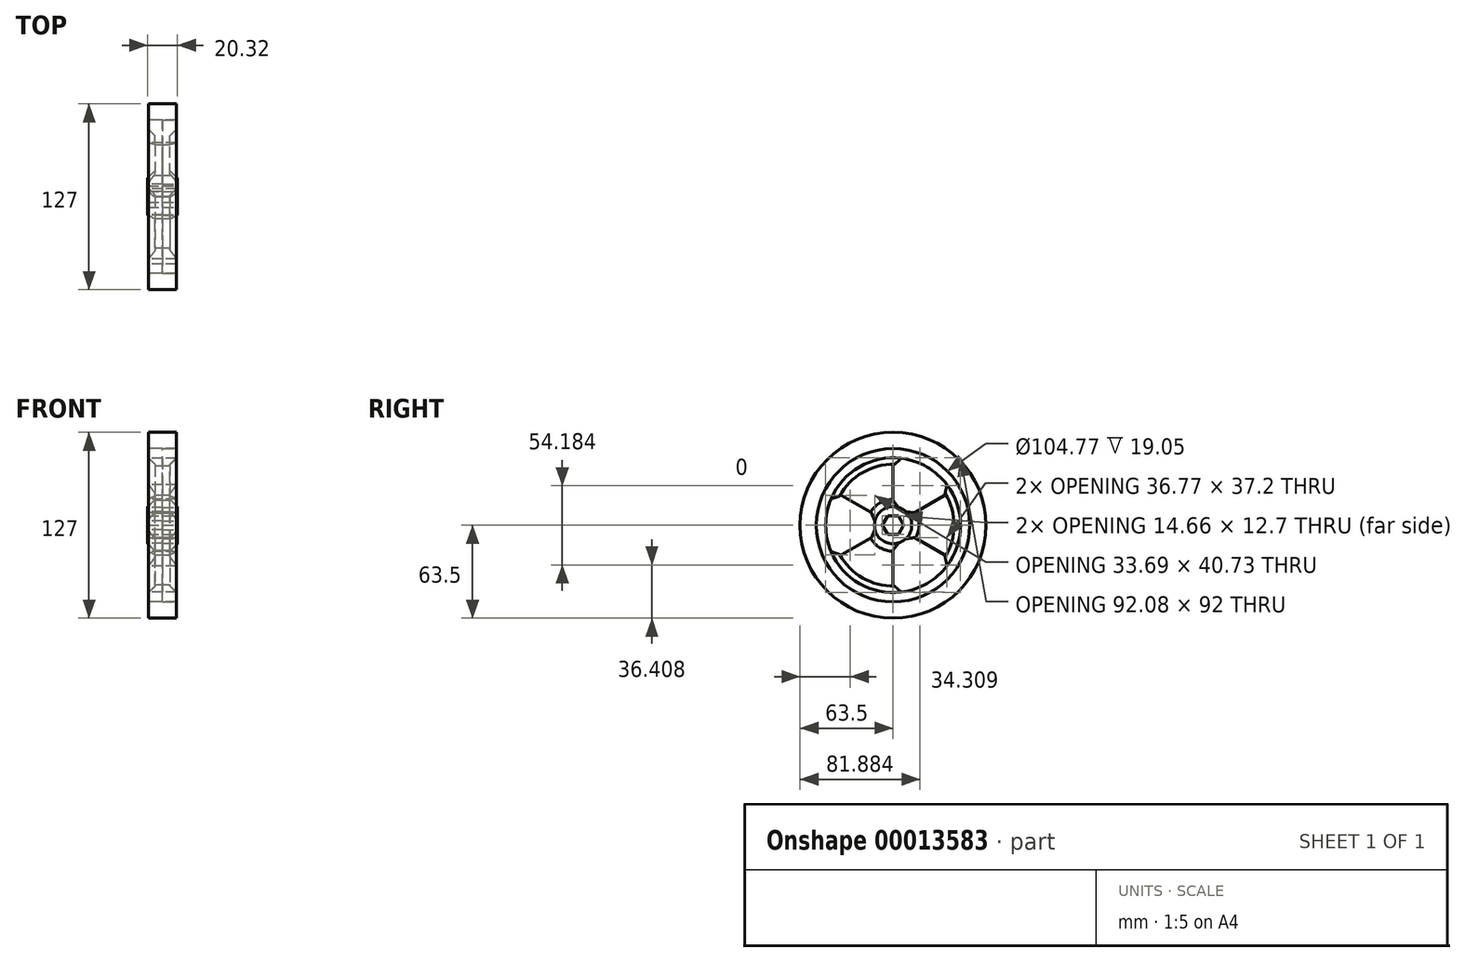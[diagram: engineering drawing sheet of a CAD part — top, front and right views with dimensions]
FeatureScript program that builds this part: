
annotation { "Feature Type Name" : "Feature", "Feature Type Description" : "" }
export const myFeature = defineFeature(function(context is Context, id is Id, definition is map)
    precondition{}
    {
        {
            var Q0;
            Q0=qCreatedBy(makeId("Front.planeOp"),FACE);
            var sketch = newSketch(context, id + "F0", { "sketchPlane" : qUnion([Q0])});
            skLineSegment(sketch, "E0", {"start": v(0, 0) * mm, "end": v(0, 52.39) * mm});
            skLineSegment(sketch, "E1", {"start": v(0, 52.39) * mm, "end": v(9.53, 52.39) * mm});
            skLineSegment(sketch, "E2", {"start": v(9.53, 52.39) * mm, "end": v(9.53, 46.04) * mm});
            skLineSegment(sketch, "E3", {"start": v(5.08, 41.6) * mm, "end": v(5.08, 12.7) * mm});
            skLineSegment(sketch, "E4", {"start": v(5.08, 12.7) * mm, "end": v(10.16, 12.7) * mm});
            skLineSegment(sketch, "E5", {"start": v(10.16, 12.7) * mm, "end": v(10.16, 0) * mm});
            skLineSegment(sketch, "E6", {"start": v(10.16, 0) * mm, "end": v(0, 0) * mm});
            skLineSegment(sketch, "E7", {"start": v(0, 0) * mm, "end": v(0, -52.39) * mm, "construction": true});
            skLineSegment(sketch, "E8", {"start": v(0, -52.39) * mm, "end": v(10.16, -52.39) * mm, "construction": true});
            skLineSegment(sketch, "E9", {"start": v(10.16, -52.39) * mm, "end": v(10.16, 0) * mm, "construction": true});
            skLineSegment(sketch, "E10", {"start": v(5.08, 41.6) * mm, "end": v(9.53, 46.04) * mm});
            skSolve(sketch);
        }
        {
            var Q0;
            Q0=makeQuery(id+"F0.imprint","IMPRINT",FACE,{"disambiguationData":[TD([[makeQuery(id+"F0.imprint","IMPRINT",EDGE,{"derivedFrom":sQuery(id+"F0.wireOp",EDGE,"E0")}),-1.0]])]});
            var Q1;
            Q1=sQuery(id+"F0.wireOp",EDGE,"E6");
            revolve(context, id + "F1", {"entities" : qUnion([Q0]), "axis" : qUnion([Q1]), "revolveType" : RevolveType.FULL});
        }
        {
            var Q0;
            Q0=makeQuery(id+"F1.opRevolve","SWEPT_BODY",BODY,{"disambiguationData":[OSD([sQuery(id+"F0.wireOp",EDGE,"E0"),sQuery(id+"F0.wireOp",EDGE,"E1"),sQuery(id+"F0.wireOp",EDGE,"E2"),sQuery(id+"F0.wireOp",EDGE,"E3"),sQuery(id+"F0.wireOp",EDGE,"E4"),sQuery(id+"F0.wireOp",EDGE,"E5"),sQuery(id+"F0.wireOp",EDGE,"E6"),sQuery(id+"F0.wireOp",EDGE,"E10")])]});
            var Q1;
            Q1=qCreatedBy(makeId("Right.planeOp"),FACE);
            mirror(context, id + "F2", {"entities" : qUnion([Q0]), "mirrorPlane" : qUnion([Q1])});
        }
        {
            var Q0;
            Q0=makeQuery(id+"F1.opRevolve","SWEPT_FACE",FACE,{"disambiguationData":[OSD([sQuery(id+"F0.wireOp",EDGE,"E5")])]});
            var sketch = newSketch(context, id + "F3", { "sketchPlane" : qUnion([Q0])});
            skCircle(sketch, "E11.cCircle", {"center": v(0, 0) * mm, "radius": 6.35 * mm, "construction": true});
            skLineSegment(sketch, "E11.0", {"start": v(3.67, -6.35) * mm, "end": v(-3.67, -6.35) * mm});
            skLineSegment(sketch, "E11.1", {"start": v(-3.67, -6.35) * mm, "end": v(-7.33, 0) * mm});
            skLineSegment(sketch, "E11.2", {"start": v(-7.33, 0) * mm, "end": v(-3.67, 6.35) * mm});
            skLineSegment(sketch, "E11.3", {"start": v(-3.67, 6.35) * mm, "end": v(3.67, 6.35) * mm});
            skLineSegment(sketch, "E11.4", {"start": v(3.67, 6.35) * mm, "end": v(7.33, 0) * mm});
            skLineSegment(sketch, "E11.5", {"start": v(7.33, 0) * mm, "end": v(3.67, -6.35) * mm});
            skPoint(sketch, "E11.0.midPoint", {"position": v(0, -6.35) * mm});
            skSolve(sketch);
        }
        {
            var Q0;
            Q0 = qSketchRegion(id + "F3", true);
            extrude(context, id + "F4", {"entities" : qUnion([Q0]), "operationType" : NewBodyOperationType.REMOVE, "endBound" : BoundingType.THROUGH_ALL, "oppositeDirection" : true, "depth" : 25.4 * mm});
        }
        {
            var Q0;
            Q0=qCreatedBy(makeId("Front.planeOp"),FACE);
            var sketch = newSketch(context, id + "F5", { "sketchPlane" : qUnion([Q0])});
            skLineSegment(sketch, "E12.bottom", {"start": v(-9.53, 52.39) * mm, "end": v(9.52, 52.39) * mm});
            skLineSegment(sketch, "E12.top", {"start": v(-9.53, 63.5) * mm, "end": v(9.52, 63.5) * mm});
            skLineSegment(sketch, "E12.left", {"start": v(-9.53, 52.39) * mm, "end": v(-9.53, 63.5) * mm});
            skLineSegment(sketch, "E12.right", {"start": v(9.53, 52.39) * mm, "end": v(9.53, 63.5) * mm});
            skLineSegment(sketch, "E13", {"start": v(0, 0) * mm, "end": v(0, -63.5) * mm, "construction": true});
            skLineSegment(sketch, "E14", {"start": v(0, -63.5) * mm, "end": v(9.53, -63.5) * mm, "construction": true});
            skLineSegment(sketch, "E15", {"start": v(9.53, -63.5) * mm, "end": v(9.53, 52.39) * mm, "construction": true});
            skLineSegment(sketch, "E16", {"start": v(0, 63.5) * mm, "end": v(0, 0) * mm, "construction": true});
            skLineSegment(sketch, "E17", {"start": v(0, 0) * mm, "end": v(9.53, 0) * mm, "construction": true});
            skSolve(sketch);
        }
        {
            var Q0;
            Q0 = qSketchRegion(id + "F5", true);
            var Q1;
            Q1=sQuery(id+"F5.wireOp",EDGE,"E17");
            revolve(context, id + "F6", {"entities" : qUnion([Q0]), "axis" : qUnion([Q1]), "revolveType" : RevolveType.FULL});
        }
        {
            var Q0;
            Q0=makeQuery(id+"F2.opPattern","COPY",FACE,{"derivedFrom":makeQuery(id+"F1.opRevolve","SWEPT_FACE",FACE,{"disambiguationData":[OSD([sQuery(id+"F0.wireOp",EDGE,"E2")])]}),"instanceName":"1"});
            var sketch = newSketch(context, id + "F7", { "sketchPlane" : qUnion([Q0])});
            skCircle(sketch, "E18.0", {"center": v(0, 0) * mm, "radius": 12.7 * mm});
            skCircle(sketch, "E19.0", {"center": v(0, 0) * mm, "radius": 46.04 * mm});
            skLineSegment(sketch, "E20", {"start": v(0, 12.7) * mm, "end": v(0, 46.04) * mm});
            skLineSegment(sketch, "E21.1.0", {"start": v(-11, 6.35) * mm, "end": v(-39.87, 23.02) * mm});
            skLineSegment(sketch, "E21.2.0", {"start": v(-11, -6.35) * mm, "end": v(-39.87, -23.02) * mm});
            skLineSegment(sketch, "E21.3.0", {"start": v(0, -12.7) * mm, "end": v(0, -46.04) * mm});
            skLineSegment(sketch, "E21.4.0", {"start": v(11, -6.35) * mm, "end": v(39.87, -23.02) * mm});
            skLineSegment(sketch, "E21.5.0", {"start": v(11, 6.35) * mm, "end": v(39.87, 23.02) * mm});
            skSolve(sketch);
        }
        {
            var Q0;
            {var subQ1=sQuery(id+"F7.wireOp",EDGE,"E20");Q0=makeQuery(id+"F7.imprint","IMPRINT",FACE,{"disambiguationData":[TD([[makeQuery(id+"F7.imprint","IMPRINT",EDGE,{"derivedFrom":subQ1}),1.0]])]});}
            var Q1;
            {var subQ1=sQuery(id+"F7.wireOp",EDGE,"E21.2.0");Q1=makeQuery(id+"F7.imprint","IMPRINT",FACE,{"disambiguationData":[TD([[makeQuery(id+"F7.imprint","IMPRINT",EDGE,{"derivedFrom":subQ1}),1.0]])]});}
            var Q2;
            {var subQ1=sQuery(id+"F7.wireOp",EDGE,"E21.4.0");Q2=makeQuery(id+"F7.imprint","IMPRINT",FACE,{"disambiguationData":[TD([[makeQuery(id+"F7.imprint","IMPRINT",EDGE,{"derivedFrom":subQ1}),1.0]])]});}
            extrude(context, id + "F8", {"entities" : qUnion([Q0, Q1, Q2]), "operationType" : NewBodyOperationType.REMOVE, "endBound" : BoundingType.THROUGH_ALL, "oppositeDirection" : true, "depth" : 25 * mm});
        }
        {
            var Q0;
            Q0=makeQuery(id+"F8.boolean.opBoolean","COPY",EDGE,{"disambiguationData":[OD(0.0)],"derivedFrom":makeQuery(id+"F8.opExtrude","SWEPT_EDGE",EDGE,{"disambiguationData":[OSD([sQuery(id+"F7.wireOp",EDGE,"E19.0"),sQuery(id+"F7.wireOp",EDGE,"E21.1.0")])]})});
            var Q1;
            Q1=makeQuery(id+"F8.boolean.opBoolean","COPY",EDGE,{"disambiguationData":[OD(1.0)],"derivedFrom":makeQuery(id+"F8.opExtrude","SWEPT_EDGE",EDGE,{"disambiguationData":[OSD([sQuery(id+"F7.wireOp",EDGE,"E19.0"),sQuery(id+"F7.wireOp",EDGE,"E21.1.0")])]})});
            var Q2;
            Q2=makeQuery(id+"F8.boolean.opBoolean","COPY",EDGE,{"disambiguationData":[OD(0.0)],"derivedFrom":makeQuery(id+"F8.opExtrude","SWEPT_EDGE",EDGE,{"disambiguationData":[OSD([sQuery(id+"F7.wireOp",EDGE,"E19.0"),sQuery(id+"F7.wireOp",EDGE,"E20")])]})});
            var Q3;
            Q3=makeQuery(id+"F8.boolean.opBoolean","COPY",EDGE,{"disambiguationData":[OD(1.0)],"derivedFrom":makeQuery(id+"F8.opExtrude","SWEPT_EDGE",EDGE,{"disambiguationData":[OSD([sQuery(id+"F7.wireOp",EDGE,"E19.0"),sQuery(id+"F7.wireOp",EDGE,"E20")])]})});
            var Q4;
            Q4=makeQuery(id+"F8.boolean.opBoolean","COPY",EDGE,{"disambiguationData":[OD(1.0)],"derivedFrom":makeQuery(id+"F8.opExtrude","SWEPT_EDGE",EDGE,{"disambiguationData":[OSD([sQuery(id+"F7.wireOp",EDGE,"E19.0"),sQuery(id+"F7.wireOp",EDGE,"E21.5.0")])]})});
            var Q5;
            Q5=makeQuery(id+"F8.boolean.opBoolean","COPY",EDGE,{"disambiguationData":[OD(0.0)],"derivedFrom":makeQuery(id+"F8.opExtrude","SWEPT_EDGE",EDGE,{"disambiguationData":[OSD([sQuery(id+"F7.wireOp",EDGE,"E19.0"),sQuery(id+"F7.wireOp",EDGE,"E21.5.0")])]})});
            var Q6;
            Q6=makeQuery(id+"F8.boolean.opBoolean","COPY",EDGE,{"disambiguationData":[OD(0.0)],"derivedFrom":makeQuery(id+"F8.opExtrude","SWEPT_EDGE",EDGE,{"disambiguationData":[OSD([sQuery(id+"F7.wireOp",EDGE,"E19.0"),sQuery(id+"F7.wireOp",EDGE,"E21.4.0")])]})});
            var Q7;
            Q7=makeQuery(id+"F8.boolean.opBoolean","COPY",EDGE,{"disambiguationData":[OD(1.0)],"derivedFrom":makeQuery(id+"F8.opExtrude","SWEPT_EDGE",EDGE,{"disambiguationData":[OSD([sQuery(id+"F7.wireOp",EDGE,"E19.0"),sQuery(id+"F7.wireOp",EDGE,"E21.4.0")])]})});
            var Q8;
            Q8=makeQuery(id+"F8.boolean.opBoolean","COPY",EDGE,{"disambiguationData":[OD(0.0)],"derivedFrom":makeQuery(id+"F8.opExtrude","SWEPT_EDGE",EDGE,{"disambiguationData":[OSD([sQuery(id+"F7.wireOp",EDGE,"E19.0"),sQuery(id+"F7.wireOp",EDGE,"E21.2.0")])]})});
            var Q9;
            Q9=makeQuery(id+"F8.boolean.opBoolean","COPY",EDGE,{"disambiguationData":[OD(1.0)],"derivedFrom":makeQuery(id+"F8.opExtrude","SWEPT_EDGE",EDGE,{"disambiguationData":[OSD([sQuery(id+"F7.wireOp",EDGE,"E19.0"),sQuery(id+"F7.wireOp",EDGE,"E21.2.0")])]})});
            var Q10;
            Q10=makeQuery(id+"F8.boolean.opBoolean","COPY",EDGE,{"disambiguationData":[OD(0.0)],"derivedFrom":makeQuery(id+"F8.opExtrude","SWEPT_EDGE",EDGE,{"disambiguationData":[OSD([sQuery(id+"F7.wireOp",EDGE,"E19.0"),sQuery(id+"F7.wireOp",EDGE,"E21.3.0")])]})});
            var Q11;
            Q11=makeQuery(id+"F8.boolean.opBoolean","COPY",EDGE,{"disambiguationData":[OD(1.0)],"derivedFrom":makeQuery(id+"F8.opExtrude","SWEPT_EDGE",EDGE,{"disambiguationData":[OSD([sQuery(id+"F7.wireOp",EDGE,"E19.0"),sQuery(id+"F7.wireOp",EDGE,"E21.3.0")])]})});
            var Q12;
            Q12=makeQuery(id+"F8.boolean.opBoolean","COPY",EDGE,{"disambiguationData":[OD(1.0)],"derivedFrom":makeQuery(id+"F8.opExtrude","SWEPT_EDGE",EDGE,{"disambiguationData":[OSD([sQuery(id+"F7.wireOp",EDGE,"E18.0"),sQuery(id+"F7.wireOp",EDGE,"E21.1.0")])]})});
            var Q13;
            Q13=makeQuery(id+"F8.boolean.opBoolean","COPY",EDGE,{"disambiguationData":[OD(0.0)],"derivedFrom":makeQuery(id+"F8.opExtrude","SWEPT_EDGE",EDGE,{"disambiguationData":[OSD([sQuery(id+"F7.wireOp",EDGE,"E18.0"),sQuery(id+"F7.wireOp",EDGE,"E21.1.0")])]})});
            var Q14;
            Q14=makeQuery(id+"F8.boolean.opBoolean","COPY",EDGE,{"disambiguationData":[OD(1.0)],"derivedFrom":makeQuery(id+"F8.opExtrude","SWEPT_EDGE",EDGE,{"disambiguationData":[OSD([sQuery(id+"F7.wireOp",EDGE,"E18.0"),sQuery(id+"F7.wireOp",EDGE,"E20")])]})});
            var Q15;
            Q15=makeQuery(id+"F8.boolean.opBoolean","COPY",EDGE,{"disambiguationData":[OD(0.0)],"derivedFrom":makeQuery(id+"F8.opExtrude","SWEPT_EDGE",EDGE,{"disambiguationData":[OSD([sQuery(id+"F7.wireOp",EDGE,"E18.0"),sQuery(id+"F7.wireOp",EDGE,"E20")])]})});
            var Q16;
            Q16=makeQuery(id+"F8.boolean.opBoolean","COPY",EDGE,{"disambiguationData":[OD(1.0)],"derivedFrom":makeQuery(id+"F8.opExtrude","SWEPT_EDGE",EDGE,{"disambiguationData":[OSD([sQuery(id+"F7.wireOp",EDGE,"E18.0"),sQuery(id+"F7.wireOp",EDGE,"E21.5.0")])]})});
            var Q17;
            Q17=makeQuery(id+"F8.boolean.opBoolean","COPY",EDGE,{"disambiguationData":[OD(0.0)],"derivedFrom":makeQuery(id+"F8.opExtrude","SWEPT_EDGE",EDGE,{"disambiguationData":[OSD([sQuery(id+"F7.wireOp",EDGE,"E18.0"),sQuery(id+"F7.wireOp",EDGE,"E21.5.0")])]})});
            var Q18;
            Q18=makeQuery(id+"F8.boolean.opBoolean","COPY",EDGE,{"disambiguationData":[OD(1.0)],"derivedFrom":makeQuery(id+"F8.opExtrude","SWEPT_EDGE",EDGE,{"disambiguationData":[OSD([sQuery(id+"F7.wireOp",EDGE,"E18.0"),sQuery(id+"F7.wireOp",EDGE,"E21.4.0")])]})});
            var Q19;
            Q19=makeQuery(id+"F8.boolean.opBoolean","COPY",EDGE,{"disambiguationData":[OD(0.0)],"derivedFrom":makeQuery(id+"F8.opExtrude","SWEPT_EDGE",EDGE,{"disambiguationData":[OSD([sQuery(id+"F7.wireOp",EDGE,"E18.0"),sQuery(id+"F7.wireOp",EDGE,"E21.4.0")])]})});
            var Q20;
            Q20=makeQuery(id+"F8.boolean.opBoolean","COPY",EDGE,{"disambiguationData":[OD(1.0)],"derivedFrom":makeQuery(id+"F8.opExtrude","SWEPT_EDGE",EDGE,{"disambiguationData":[OSD([sQuery(id+"F7.wireOp",EDGE,"E18.0"),sQuery(id+"F7.wireOp",EDGE,"E21.2.0")])]})});
            var Q21;
            Q21=makeQuery(id+"F8.boolean.opBoolean","COPY",EDGE,{"disambiguationData":[OD(0.0)],"derivedFrom":makeQuery(id+"F8.opExtrude","SWEPT_EDGE",EDGE,{"disambiguationData":[OSD([sQuery(id+"F7.wireOp",EDGE,"E18.0"),sQuery(id+"F7.wireOp",EDGE,"E21.2.0")])]})});
            var Q22;
            Q22=makeQuery(id+"F8.boolean.opBoolean","COPY",EDGE,{"disambiguationData":[OD(1.0)],"derivedFrom":makeQuery(id+"F8.opExtrude","SWEPT_EDGE",EDGE,{"disambiguationData":[OSD([sQuery(id+"F7.wireOp",EDGE,"E18.0"),sQuery(id+"F7.wireOp",EDGE,"E21.3.0")])]})});
            var Q23;
            Q23=makeQuery(id+"F8.boolean.opBoolean","COPY",EDGE,{"disambiguationData":[OD(0.0)],"derivedFrom":makeQuery(id+"F8.opExtrude","SWEPT_EDGE",EDGE,{"disambiguationData":[OSD([sQuery(id+"F7.wireOp",EDGE,"E18.0"),sQuery(id+"F7.wireOp",EDGE,"E21.3.0")])]})});
            var Q24;
            {var subQ0=sQuery(id+"F0.wireOp",EDGE,"E3");var subQ1=sQuery(id+"F0.wireOp",EDGE,"E4");var subQ3=sQuery(id+"F7.wireOp",EDGE,"E21.1.0");Q24=makeQuery(id+"F8.boolean.opBoolean","SPLIT",EDGE,{"disambiguationData":[TD([makeQuery(id+"F8.opExtrude","SWEPT_FACE",FACE,{"disambiguationData":[OSD([subQ3])]})])],"derivedFrom":makeQuery(id+"F2.opPattern","COPY",EDGE,{"derivedFrom":makeQuery(id+"F1.opRevolve","SWEPT_EDGE",EDGE,{"disambiguationData":[OSD([subQ0,subQ1])]}),"instanceName":"1"})});}
            var Q25;
            {var subQ0=sQuery(id+"F0.wireOp",EDGE,"E3");var subQ1=sQuery(id+"F0.wireOp",EDGE,"E4");var subQ3=sQuery(id+"F7.wireOp",EDGE,"E21.3.0");Q25=makeQuery(id+"F8.boolean.opBoolean","SPLIT",EDGE,{"disambiguationData":[TD([makeQuery(id+"F8.opExtrude","SWEPT_FACE",FACE,{"disambiguationData":[OSD([subQ3])]})])],"derivedFrom":makeQuery(id+"F2.opPattern","COPY",EDGE,{"derivedFrom":makeQuery(id+"F1.opRevolve","SWEPT_EDGE",EDGE,{"disambiguationData":[OSD([subQ0,subQ1])]}),"instanceName":"1"})});}
            var Q26;
            {var subQ0=sQuery(id+"F0.wireOp",EDGE,"E3");var subQ1=sQuery(id+"F0.wireOp",EDGE,"E4");var subQ2=sQuery(id+"F7.wireOp",EDGE,"E20");Q26=makeQuery(id+"F8.boolean.opBoolean","SPLIT",EDGE,{"disambiguationData":[TD([makeQuery(id+"F8.opExtrude","SWEPT_FACE",FACE,{"disambiguationData":[OSD([subQ2])]})])],"derivedFrom":makeQuery(id+"F2.opPattern","COPY",EDGE,{"derivedFrom":makeQuery(id+"F1.opRevolve","SWEPT_EDGE",EDGE,{"disambiguationData":[OSD([subQ0,subQ1])]}),"instanceName":"1"})});}
            var Q27;
            {var subQ0=sQuery(id+"F0.wireOp",EDGE,"E3");var subQ1=sQuery(id+"F0.wireOp",EDGE,"E4");var subQ4=sQuery(id+"F7.wireOp",EDGE,"E20");Q27=makeQuery(id+"F8.boolean.opBoolean","SPLIT",EDGE,{"disambiguationData":[TD([makeQuery(id+"F8.opExtrude","SWEPT_FACE",FACE,{"disambiguationData":[OSD([subQ4])]})])],"derivedFrom":makeQuery(id+"F1.opRevolve","SWEPT_EDGE",EDGE,{"disambiguationData":[OSD([subQ0,subQ1])]})});}
            var Q28;
            {var subQ0=sQuery(id+"F0.wireOp",EDGE,"E3");var subQ1=sQuery(id+"F0.wireOp",EDGE,"E4");var subQ3=sQuery(id+"F7.wireOp",EDGE,"E21.1.0");Q28=makeQuery(id+"F8.boolean.opBoolean","SPLIT",EDGE,{"disambiguationData":[TD([makeQuery(id+"F8.opExtrude","SWEPT_FACE",FACE,{"disambiguationData":[OSD([subQ3])]})])],"derivedFrom":makeQuery(id+"F1.opRevolve","SWEPT_EDGE",EDGE,{"disambiguationData":[OSD([subQ0,subQ1])]})});}
            var Q29;
            {var subQ0=sQuery(id+"F0.wireOp",EDGE,"E3");var subQ1=sQuery(id+"F0.wireOp",EDGE,"E4");var subQ3=sQuery(id+"F7.wireOp",EDGE,"E21.3.0");Q29=makeQuery(id+"F8.boolean.opBoolean","SPLIT",EDGE,{"disambiguationData":[TD([makeQuery(id+"F8.opExtrude","SWEPT_FACE",FACE,{"disambiguationData":[OSD([subQ3])]})])],"derivedFrom":makeQuery(id+"F1.opRevolve","SWEPT_EDGE",EDGE,{"disambiguationData":[OSD([subQ0,subQ1])]})});}
            chamfer(context, id + "F9", {"entities" : qUnion([Q0, Q1, Q2, Q3, Q4, Q5, Q6, Q7, Q8, Q9, Q10, Q11, Q12, Q13, Q14, Q15, Q16, Q17, Q18, Q19, Q20, Q21, Q22, Q23, Q24, Q25, Q26, Q27, Q28, Q29]), "width" : 5 * mm, "tangentPropagation" : true});
        }
    });
